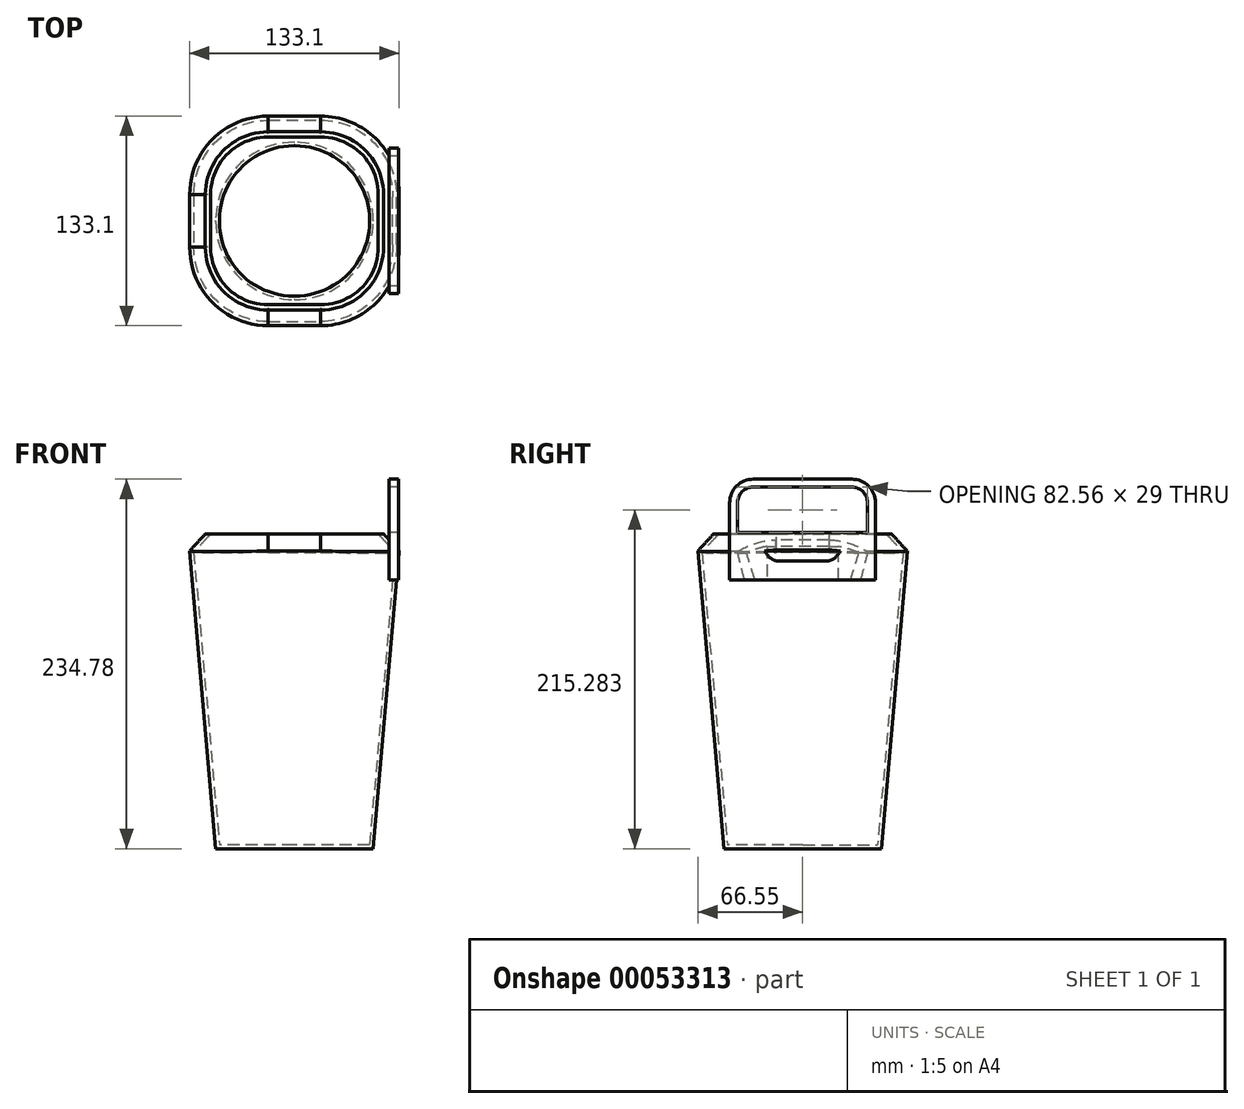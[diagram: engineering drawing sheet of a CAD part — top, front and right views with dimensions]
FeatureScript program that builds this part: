
annotation { "Feature Type Name" : "Feature", "Feature Type Description" : "" }
export const myFeature = defineFeature(function(context is Context, id is Id, definition is map)
    precondition{}
    {
        {
            var Q0;
            Q0=qCreatedBy(makeId("Top.planeOp"),FACE);
            var sketch = newSketch(context, id + "F0", { "sketchPlane" : qUnion([Q0])});
            skLineSegment(sketch, "E0.rect.bottom", {"start": v(50, -50) * mm, "end": v(-50, -50) * mm});
            skLineSegment(sketch, "E0.rect.top", {"start": v(50, 50) * mm, "end": v(-50, 50) * mm});
            skLineSegment(sketch, "E0.rect.left", {"start": v(50, -50) * mm, "end": v(50, 50) * mm});
            skLineSegment(sketch, "E0.rect.right", {"start": v(-50, -50) * mm, "end": v(-50, 50) * mm});
            skPoint(sketch, "E0.rect.middle", {"position": v(0, 0) * mm});
            skSolve(sketch);
        }
        {
            var Q0;
            Q0=makeQuery(id+"F0.imprint","IMPRINT",FACE,{"disambiguationData":[TD([[makeQuery(id+"F0.imprint","IMPRINT",EDGE,{"derivedFrom":sQuery(id+"F0.wireOp",EDGE,"E0.rect.bottom")}),-1.0]])]});
            extrude(context, id + "F1", {"entities" : qUnion([Q0]), "depth" : 200 * mm, "hasDraft" : true, "draftAngle" : 5 * degree});
        }
        {
            var Q0;
            Q0=makeQuery(id+"F1.opExtrude","SWEPT_EDGE",EDGE,{"disambiguationData":[OSD([sQuery(id+"F0.wireOp",EDGE,"E0.rect.top"),sQuery(id+"F0.wireOp",EDGE,"E0.rect.left")])]});
            var Q1;
            Q1=makeQuery(id+"F1.opExtrude","SWEPT_EDGE",EDGE,{"disambiguationData":[OSD([sQuery(id+"F0.wireOp",EDGE,"E0.rect.top"),sQuery(id+"F0.wireOp",EDGE,"E0.rect.right")])]});
            var Q2;
            Q2=makeQuery(id+"F1.opExtrude","SWEPT_EDGE",EDGE,{"disambiguationData":[OSD([sQuery(id+"F0.wireOp",EDGE,"E0.rect.bottom"),sQuery(id+"F0.wireOp",EDGE,"E0.rect.right")])]});
            var Q3;
            Q3=makeQuery(id+"F1.opExtrude","SWEPT_EDGE",EDGE,{"disambiguationData":[OSD([sQuery(id+"F0.wireOp",EDGE,"E0.rect.bottom"),sQuery(id+"F0.wireOp",EDGE,"E0.rect.left")])]});
            fillet(context, id + "F2", {"entities" : qUnion([Q0, Q1, Q2, Q3]), "radius" : 50 * mm, "tangentPropagation" : true, "allowEdgeOverflow" : false});
        }
        {
            var Q0;
            Q0=makeQuery(id+"F1.opExtrude","CAP_FACE",FACE,{"disambiguationData":[OSD([sQuery(id+"F0.wireOp",EDGE,"E0.rect.bottom"),sQuery(id+"F0.wireOp",EDGE,"E0.rect.top"),sQuery(id+"F0.wireOp",EDGE,"E0.rect.left"),sQuery(id+"F0.wireOp",EDGE,"E0.rect.right")])],"isStart":false});
            chamfer(context, id + "F3", {"entities" : qUnion([Q0]), "width" : 10 * mm, "tangentPropagation" : true});
        }
        {
            var Q0;
            Q0=makeQuery(id+"F1.opExtrude","CAP_FACE",FACE,{"disambiguationData":[OSD([sQuery(id+"F0.wireOp",EDGE,"E0.rect.bottom"),sQuery(id+"F0.wireOp",EDGE,"E0.rect.top"),sQuery(id+"F0.wireOp",EDGE,"E0.rect.left"),sQuery(id+"F0.wireOp",EDGE,"E0.rect.right")])],"isStart":false});
            shell(context, id + "F4", {"entities" : qUnion([Q0]), "thickness" : 2.5 * mm});
        }
        {
            var Q0;
            Q0=qCreatedBy(makeId("Right.planeOp"),FACE);
            cPlane(context, id + "F5", {"entities" : qUnion([Q0]), "cplaneType" : CPlaneType.OFFSET, "offset" : 60 * mm, "width" : 150 * mm, "height" : 150 * mm});
        }
        {
            var Q0;
            Q0=qCreatedBy(id+"F5.planeOp",FACE);
            var sketch = newSketch(context, id + "F6", { "sketchPlane" : qUnion([Q0])});
            skLineSegment(sketch, "E1.rect.bottom", {"start": v(46.28, 195.78) * mm, "end": v(-46.28, 195.78) * mm});
            skLineSegment(sketch, "E1.rect.top", {"start": v(31.28, 234.78) * mm, "end": v(-31.28, 234.78) * mm});
            skLineSegment(sketch, "E1.rect.left", {"start": v(46.28, 195.78) * mm, "end": v(46.28, 219.78) * mm});
            skLineSegment(sketch, "E1.rect.right", {"start": v(-46.28, 195.78) * mm, "end": v(-46.28, 219.78) * mm});
            skPoint(sketch, "E1.rect.middle", {"position": v(0, 215.28) * mm});
            skPoint(sketch, "E2.visualSharp", {"position": v(-46.28, 234.78) * mm});
            skArc(sketch, "E2.filletArc", {"start": v(-31.28, 234.78) * mm, "mid": v(-41.88, 230.39) * mm, "end": v(-46.28, 219.78) * mm});
            skPoint(sketch, "E3.visualSharp", {"position": v(46.28, 234.78) * mm});
            skArc(sketch, "E3.filletArc", {"start": v(46.28, 219.78) * mm, "mid": v(41.88, 230.39) * mm, "end": v(31.28, 234.78) * mm});
            skArc(sketch, "E4.0", {"start": v(41.28, 219.78) * mm, "mid": v(38.35, 226.85) * mm, "end": v(31.28, 229.78) * mm});
            skArc(sketch, "E4.1", {"start": v(-31.28, 229.78) * mm, "mid": v(-38.35, 226.85) * mm, "end": v(-41.28, 219.78) * mm});
            skLineSegment(sketch, "E4.2", {"start": v(-41.28, 200.78) * mm, "end": v(-41.28, 219.78) * mm});
            skLineSegment(sketch, "E4.3", {"start": v(31.28, 229.78) * mm, "end": v(-31.28, 229.78) * mm});
            skLineSegment(sketch, "E4.4", {"start": v(41.28, 200.78) * mm, "end": v(-41.28, 200.78) * mm});
            skLineSegment(sketch, "E4.5", {"start": v(41.28, 200.78) * mm, "end": v(41.28, 219.78) * mm});
            skSolve(sketch);
        }
        {
            var Q0;
            Q0=makeQuery(id+"F6.imprint","IMPRINT",FACE,{"disambiguationData":[TD([[makeQuery(id+"F6.imprint","IMPRINT",EDGE,{"derivedFrom":sQuery(id+"F6.wireOp",EDGE,"E1.rect.bottom")}),-1.0]])]});
            extrude(context, id + "F7", {"entities" : qUnion([Q0]), "operationType" : NewBodyOperationType.ADD, "depth" : 6 * mm});
        }
        {
            var Q0;
            Q0=makeQuery(id+"F7.opExtrude","SWEPT_FACE",FACE,{"disambiguationData":[OSD([sQuery(id+"F6.wireOp",EDGE,"E1.rect.bottom")])]});
            extrude(context, id + "F8", {"entities" : qUnion([Q0]), "operationType" : NewBodyOperationType.ADD, "depth" : 25 * mm});
        }
    });
